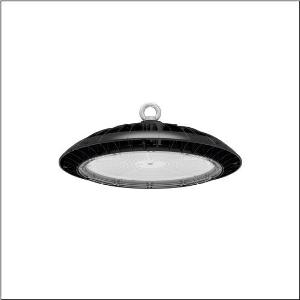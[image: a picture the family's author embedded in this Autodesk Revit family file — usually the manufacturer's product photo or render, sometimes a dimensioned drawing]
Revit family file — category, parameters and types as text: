
# Revit family: highbay_42-l_51hp32mb7mma
name_source: partatom
category: Lighting Fixtures
units: mm (PartAtom-declared; Revit-internal decimal feet)

## family parameters
Cut with Voids When Loaded = No
Host = Face
Light Source = No
Part Type = Normal
Room Calculation Point = No
Round Connector Dimension = Use Diameter
Shared = No

## types (1)
- --- (1 x LED, 28000 lm, 175 W, 5700K)
    Apparent Load = 175 VA
    CIE Flux Codes = 49 82 98 100 100
    Color Rendering = 80
    Color Temperature = 5700K
    Default Elevation = 1800 mm
    Description = Highbay 42-L, LED high bay luminaire, primary light control with lens, of PC, primary optical cover: cover panel, of PC, transparent, light emission: direct distribution, primary light characteristic: rotationally symmetric, installation type: suspended mounting, surface-mounted, LED, rated luminous flux: 28.000lm, luminous efficacy: 160lm/W, light colour: 857, colour temperature: 5700K, control gear: ECG, with cable, 3x 1.0mm², free wire ends, mains connection: 230V, AC, 50Hz, cable length: 1,5m, rated input power: 175W, housing, rotationally symmetric, of diecast aluminium, black, with hook on luminaire side, diameter: 305mm, height: 117mm, protection rating (complete): IP65, insulation class (complete): insulation class I (protective earthing), certification: CE, UKCA, protection symbol: D, impact resistance: IK08, permissible operating ambient temperature: -20..+40°C, corresponds to IFS (International Featured Standards) requirements for safety and quality in the food industry, packaging unit: 1 piece
    Height = 117 mm
    Lamp = 1 x LED
    Lamp Light Flux = 28000 lm
    Lamp Power = 175 W
    Lamp count = 1
    Length = 305 mm
    Luminous efficacy = 160 lm/W
    Manufacturer = Siteco
    ModVariant = No
    Model = 51HP32MB7MMA
    Mounting Place = Ceiling
    Mounting Type = Pendant
    Number of Poles = 1
    OnlyDefault = Yes
    Power Factor = 1
    Product Name = Highbay 42-L
    Product group = LED high bay luminaire
    ProductGroupID = 903
    Protection Class = Protection class I
    Protection Degree = IP 65
    RLX_Detail_Level = 1
    RLX_Emergency_Light_Flux = 0 lm
    RLX_Emergency_Type = 0
    RLX_Emergency_Type_DB = No
    RlxData = <blob elided: 286077 chars, md5=c92c4c37>
    Socket = socket
    Standby Power = 0 W
    System Light Flux = 28000 lm
    System Power = 175 W
    Type Comments = factory setting: luminous flux: 100 % | (OFF | OFF | OFF)
    Type Image = l_1003932.jpg
    URL = http://relux.com
    VarID = @adj_171721
    Voltage = 0 V
    Weight = 0.00 kg
    Width = 0 mm  [stored 0 ft]

note: [stored X ft] marks values corroborated as IEEE doubles in the binary element streams (Revit-internal decimal feet)

## geometry (parser evidence)
native form markers: Blend x4, Sweep x12
no freeform markers — native parametric forms only
